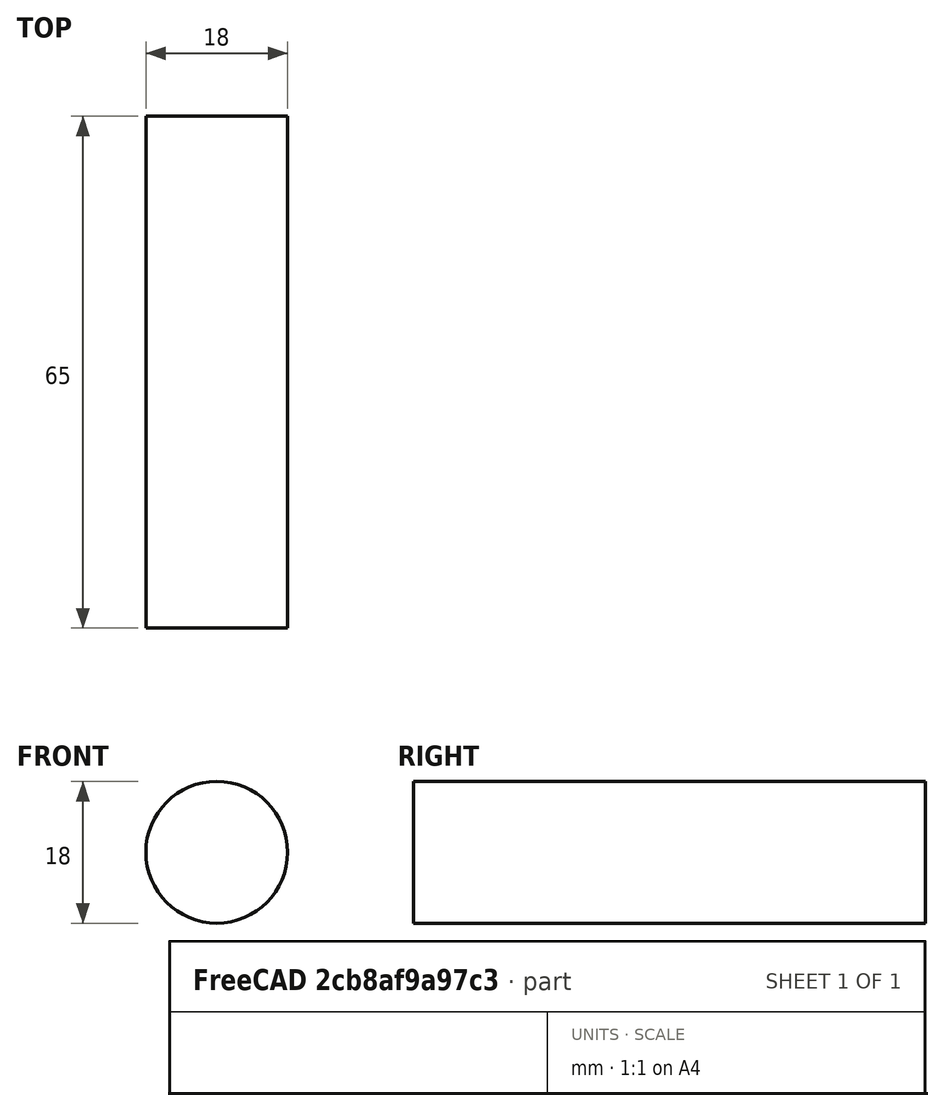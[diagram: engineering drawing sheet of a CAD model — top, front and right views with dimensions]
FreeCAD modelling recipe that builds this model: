
FCSTD DOCUMENT  (FreeCAD 1.0R39109 (Git))
Label: 18650
License: All rights reserved
LicenseURL: http://en.wikipedia.org/wiki/All_rights_reserved
objects: Sketcher::SketchObject×1, PartDesign::Pad×1, PartDesign::Body×1, App::Part×1
note: 6 computed .brp shape members not serialized (recipe doc carries the construction recipe); baked Part::Feature solids carry a one-line shape summary decoded from their .brp

FEATURE [Sketcher::SketchObject] Sketch
  ArcFitTolerance = 1e-06
  AttachmentSupport = -> [XZ_Plane001]
  FullyConstrained = true
  MakeInternals = false
  MapMode = 5
  Placement = pos=(0,0,0) rot=(1,0,0;1.5708rad)
  sketch-geometry (1):
    g0: Circle CenterX=0 CenterY=0 CenterZ=0 NormalX=0 NormalY=0 NormalZ=1 AngleXU=0 Radius=9
  constraints (2):
    c: Coincident(g0,g-1)
    c: Diameter(g0) = 18
FEATURE [PartDesign::Pad] Pad
  Direction = (0,-1,2e-16)
  Length = 65
  Length2 = 10
  Placement = pos=(0,0,0) rot=(1,0,0;1.5708rad)
  Profile = -> Sketch
  ReferenceAxis = -> Sketch [N_Axis]
  Refine = true
  Suppressed = false
  Type = 0
FEATURE [PartDesign::Body] Body  label="18650001"
  AllowCompound = false
  Group = -> [Sketch,Pad]
  Origin = -> Origin001
  Tip = -> Pad
FEATURE [App::Part] Part  label="18650"
  Group = -> [Body]
  Origin = -> Origin
